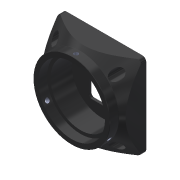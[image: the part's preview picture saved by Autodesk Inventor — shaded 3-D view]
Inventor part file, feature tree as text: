
AUTODESK INVENTOR PART (.ipt)
format: ipt  version: 2019 (Build 230136000, 136)  size: 424,960 bytes
history: native  units: in
note: dims shown in document units (in); Inventor stores cm internally (conversion verified against a paired STEP export)
features: fillet x1
ambient origin geometry x8: Origin, YZ Plane, XZ Plane, XY Plane, X Axis, Y Axis, Z Axis, Center Point
bodies: Solid1 (feature_tree)
feature tree (1):
  fillet  "Fillet5"  [1 undecoded]
note: 1 required parameter value undecoded (feature->parameter linkage not recoverable at this tier; creation-order binding heuristic only, values carry confidence <= 0.55)
